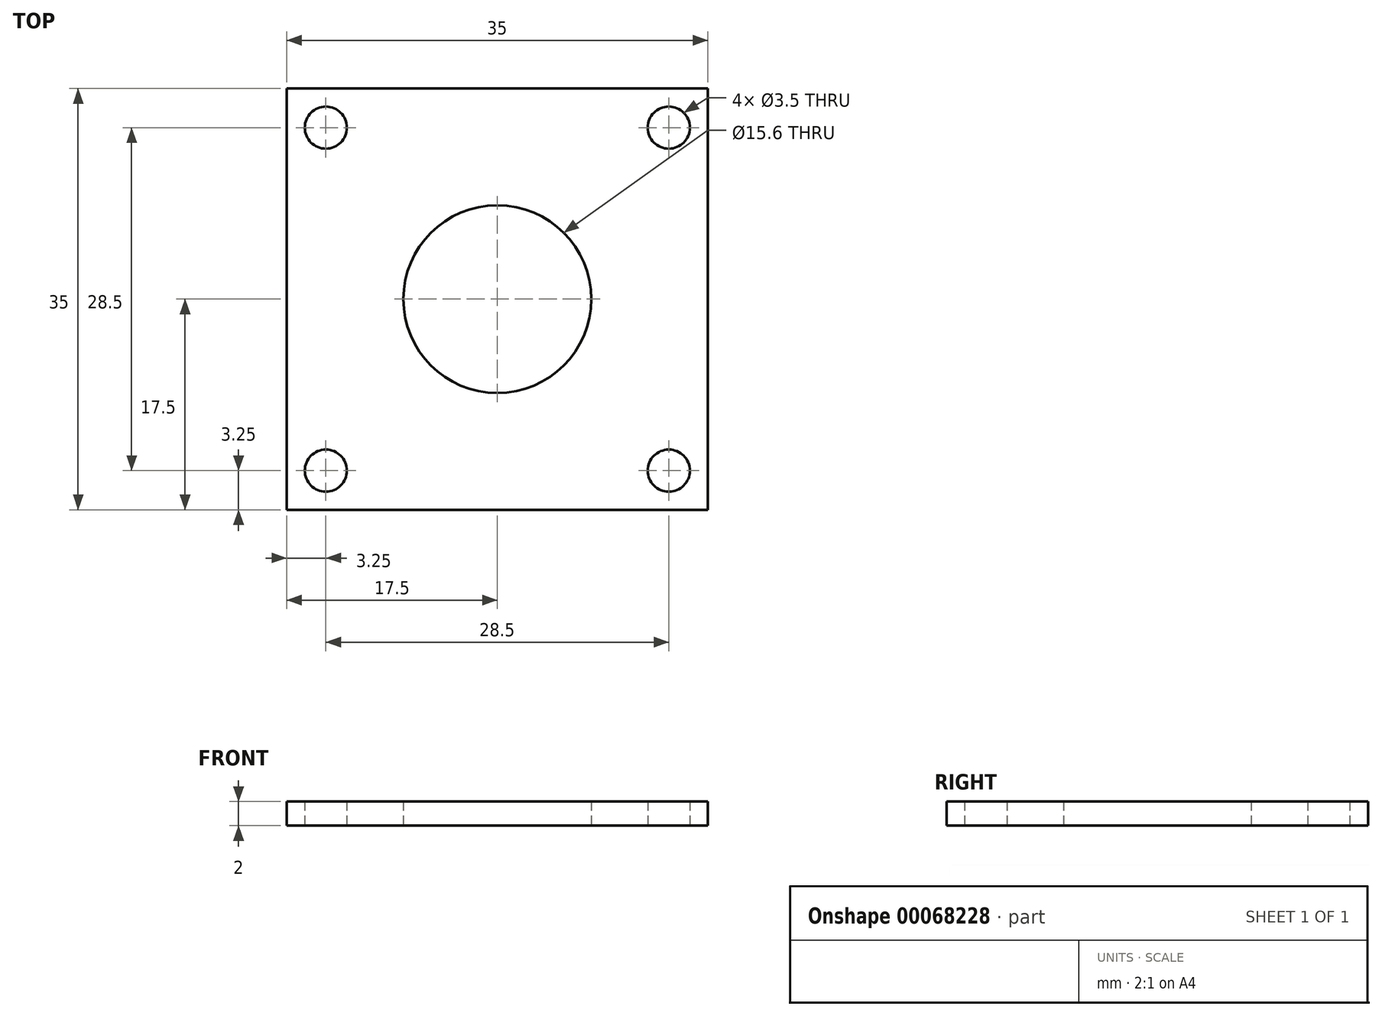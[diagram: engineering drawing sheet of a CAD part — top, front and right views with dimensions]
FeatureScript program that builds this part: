
annotation { "Feature Type Name" : "Feature", "Feature Type Description" : "" }
export const myFeature = defineFeature(function(context is Context, id is Id, definition is map)
    precondition{}
    {
        {
            var Q0;
            Q0=qCreatedBy(makeId("Top.planeOp"),FACE);
            var sketch = newSketch(context, id + "F0", { "sketchPlane" : qUnion([Q0])});
            skCircle(sketch, "E0", {"center": v(0, 0) * mm, "radius": 7.8 * mm});
            skLineSegment(sketch, "E1.bottom", {"start": v(-17.5, 17.5) * mm, "end": v(17.5, 17.5) * mm});
            skLineSegment(sketch, "E1.top", {"start": v(-17.5, -17.5) * mm, "end": v(17.5, -17.5) * mm});
            skLineSegment(sketch, "E1.left", {"start": v(-17.5, 17.5) * mm, "end": v(-17.5, -17.5) * mm});
            skLineSegment(sketch, "E1.right", {"start": v(17.5, 17.5) * mm, "end": v(17.5, -17.5) * mm});
            skCircle(sketch, "E2", {"center": v(-14.25, 14.25) * mm, "radius": 1.75 * mm});
            skCircle(sketch, "E3.MirrorC", {"center": v(14.25, 14.25) * mm, "radius": 1.75 * mm});
            skCircle(sketch, "E4.MirrorC", {"center": v(-14.25, -14.25) * mm, "radius": 1.75 * mm});
            skCircle(sketch, "E5.MirrorC", {"center": v(14.25, -14.25) * mm, "radius": 1.75 * mm});
            skSolve(sketch);
        }
        {
            var Q0;
            Q0=makeQuery(id+"F0.imprint","IMPRINT",FACE,{"disambiguationData":[TD([[makeQuery(id+"F0.imprint","IMPRINT",EDGE,{"derivedFrom":sQuery(id+"F0.wireOp",EDGE,"E0")}),-1.0]])]});
            extrude(context, id + "F1", {"entities" : qUnion([Q0]), "depth" : 2 * mm});
        }
    });
